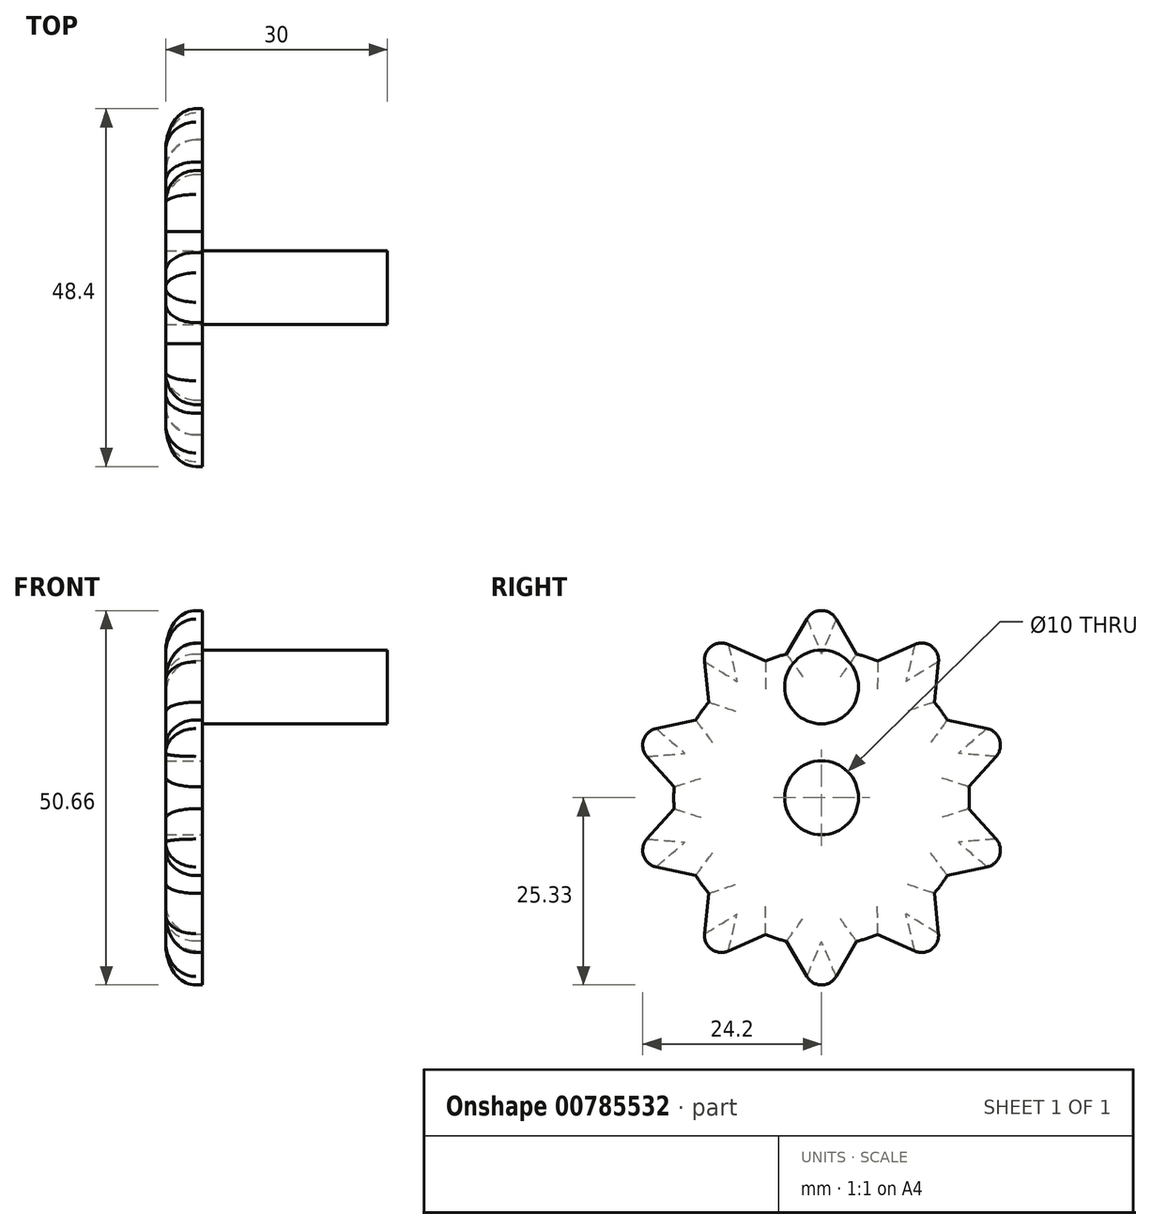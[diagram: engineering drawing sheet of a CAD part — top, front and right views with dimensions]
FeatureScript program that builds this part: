
annotation { "Feature Type Name" : "Feature", "Feature Type Description" : "" }
export const myFeature = defineFeature(function(context is Context, id is Id, definition is map)
    precondition{}
    {
        {
            var Q0;
            Q0=qCreatedBy(makeId("Right.planeOp"),FACE);
            var sketch = newSketch(context, id + "F0", { "sketchPlane" : qUnion([Q0])});
            skCircle(sketch, "E0", {"center": v(0, 0) * mm, "radius": 5 * mm});
            skCircle(sketch, "E1", {"center": v(0, 0) * mm, "radius": 20 * mm});
            skSolve(sketch);
        }
        {
            var Q0;
            Q0 = qSketchRegion(id + "F0", true);
            extrude(context, id + "F1", {"entities" : qUnion([Q0]), "depth" : 5 * mm, "offsetDistance" : 25 * mm});
        }
        {
            var Q0;
            Q0=makeQuery(id+"F1.opExtrude","CAP_FACE",FACE,{"disambiguationData":[OSD([sQuery(id+"F0.wireOp",EDGE,"E0"),sQuery(id+"F0.wireOp",EDGE,"E1")])],"isStart":false});
            var sketch = newSketch(context, id + "F2", { "sketchPlane" : qUnion([Q0])});
            skLineSegment(sketch, "E2", {"start": v(-5, 19) * mm, "end": v(-1.99, 24.19) * mm});
            skLineSegment(sketch, "E3", {"start": v(-1.99, 24.19) * mm, "end": v(1.99, 24.19) * mm, "construction": true});
            skLineSegment(sketch, "E4", {"start": v(1.99, 24.19) * mm, "end": v(5, 19) * mm});
            skArc(sketch, "E5", {"start": v(1.99, 24.19) * mm, "mid": v(0, 25.33) * mm, "end": v(-1.99, 24.19) * mm});
            skPoint(sketch, "E6", {"position": v(0, 25.33) * mm});
            skLineSegment(sketch, "E7", {"start": v(5, 19) * mm, "end": v(6.17, 19) * mm});
            skLineSegment(sketch, "E8", {"start": v(-5, 19) * mm, "end": v(-6.17, 19) * mm});
            skLineSegment(sketch, "E9.1.0", {"start": v(-12.61, 20.73) * mm, "end": v(-7.12, 18.31) * mm});
            skLineSegment(sketch, "E9.1.1", {"start": v(-15.82, 18.4) * mm, "end": v(-12.61, 20.73) * mm, "construction": true});
            skLineSegment(sketch, "E9.1.2", {"start": v(-15.21, 12.43) * mm, "end": v(-15.82, 18.4) * mm});
            skArc(sketch, "E9.1.3", {"start": v(-12.61, 20.73) * mm, "mid": v(-14.89, 20.5) * mm, "end": v(-15.82, 18.4) * mm});
            skLineSegment(sketch, "E9.1.4", {"start": v(-7.12, 18.31) * mm, "end": v(-6.17, 19) * mm});
            skPoint(sketch, "E9.1.5", {"position": v(-14.89, 20.5) * mm});
            skLineSegment(sketch, "E9.1.6", {"start": v(-15.21, 12.43) * mm, "end": v(-16.17, 11.74) * mm});
            skLineSegment(sketch, "E9.2.0", {"start": v(-22.4, 9.36) * mm, "end": v(-16.52, 10.63) * mm});
            skLineSegment(sketch, "E9.2.1", {"start": v(-23.62, 5.59) * mm, "end": v(-22.4, 9.36) * mm, "construction": true});
            skLineSegment(sketch, "E9.2.2", {"start": v(-19.62, 1.12) * mm, "end": v(-23.62, 5.59) * mm});
            skArc(sketch, "E9.2.3", {"start": v(-22.4, 9.36) * mm, "mid": v(-24.09, 7.83) * mm, "end": v(-23.62, 5.59) * mm});
            skLineSegment(sketch, "E9.2.4", {"start": v(-16.52, 10.63) * mm, "end": v(-16.17, 11.74) * mm});
            skPoint(sketch, "E9.2.5", {"position": v(-24.09, 7.83) * mm});
            skLineSegment(sketch, "E9.2.6", {"start": v(-19.62, 1.12) * mm, "end": v(-19.98, 0) * mm});
            skLineSegment(sketch, "E9.3.0", {"start": v(-23.62, -5.59) * mm, "end": v(-19.62, -1.12) * mm});
            skLineSegment(sketch, "E9.3.1", {"start": v(-22.4, -9.36) * mm, "end": v(-23.62, -5.59) * mm, "construction": true});
            skLineSegment(sketch, "E9.3.2", {"start": v(-16.52, -10.63) * mm, "end": v(-22.4, -9.36) * mm});
            skArc(sketch, "E9.3.3", {"start": v(-23.62, -5.59) * mm, "mid": v(-24.09, -7.83) * mm, "end": v(-22.4, -9.36) * mm});
            skLineSegment(sketch, "E9.3.4", {"start": v(-19.62, -1.12) * mm, "end": v(-19.98, 0) * mm});
            skPoint(sketch, "E9.3.5", {"position": v(-24.09, -7.83) * mm});
            skLineSegment(sketch, "E9.3.6", {"start": v(-16.52, -10.63) * mm, "end": v(-16.17, -11.74) * mm});
            skLineSegment(sketch, "E9.4.0", {"start": v(-15.82, -18.4) * mm, "end": v(-15.21, -12.43) * mm});
            skLineSegment(sketch, "E9.4.1", {"start": v(-12.61, -20.73) * mm, "end": v(-15.82, -18.4) * mm, "construction": true});
            skLineSegment(sketch, "E9.4.2", {"start": v(-7.12, -18.31) * mm, "end": v(-12.61, -20.73) * mm});
            skArc(sketch, "E9.4.3", {"start": v(-15.82, -18.4) * mm, "mid": v(-14.89, -20.5) * mm, "end": v(-12.61, -20.73) * mm});
            skLineSegment(sketch, "E9.4.4", {"start": v(-15.21, -12.43) * mm, "end": v(-16.17, -11.74) * mm});
            skPoint(sketch, "E9.4.5", {"position": v(-14.89, -20.5) * mm});
            skLineSegment(sketch, "E9.4.6", {"start": v(-7.12, -18.31) * mm, "end": v(-6.17, -19) * mm});
            skLineSegment(sketch, "E9.5.0", {"start": v(-1.99, -24.19) * mm, "end": v(-5, -19) * mm});
            skLineSegment(sketch, "E9.5.1", {"start": v(1.99, -24.19) * mm, "end": v(-1.99, -24.19) * mm, "construction": true});
            skLineSegment(sketch, "E9.5.2", {"start": v(5, -19) * mm, "end": v(1.99, -24.19) * mm});
            skArc(sketch, "E9.5.3", {"start": v(-1.99, -24.19) * mm, "mid": v(0, -25.33) * mm, "end": v(1.99, -24.19) * mm});
            skLineSegment(sketch, "E9.5.4", {"start": v(-5, -19) * mm, "end": v(-6.17, -19) * mm});
            skPoint(sketch, "E9.5.5", {"position": v(0, -25.33) * mm});
            skLineSegment(sketch, "E9.5.6", {"start": v(5, -19) * mm, "end": v(6.17, -19) * mm});
            skLineSegment(sketch, "E9.6.0", {"start": v(12.61, -20.73) * mm, "end": v(7.12, -18.31) * mm});
            skLineSegment(sketch, "E9.6.1", {"start": v(15.82, -18.4) * mm, "end": v(12.61, -20.73) * mm, "construction": true});
            skLineSegment(sketch, "E9.6.2", {"start": v(15.21, -12.43) * mm, "end": v(15.82, -18.4) * mm});
            skArc(sketch, "E9.6.3", {"start": v(12.61, -20.73) * mm, "mid": v(14.89, -20.5) * mm, "end": v(15.82, -18.4) * mm});
            skLineSegment(sketch, "E9.6.4", {"start": v(7.12, -18.31) * mm, "end": v(6.17, -19) * mm});
            skPoint(sketch, "E9.6.5", {"position": v(14.89, -20.5) * mm});
            skLineSegment(sketch, "E9.6.6", {"start": v(15.21, -12.43) * mm, "end": v(16.17, -11.74) * mm});
            skLineSegment(sketch, "E9.7.0", {"start": v(22.4, -9.36) * mm, "end": v(16.52, -10.63) * mm});
            skLineSegment(sketch, "E9.7.1", {"start": v(23.62, -5.59) * mm, "end": v(22.4, -9.36) * mm, "construction": true});
            skLineSegment(sketch, "E9.7.2", {"start": v(19.62, -1.12) * mm, "end": v(23.62, -5.59) * mm});
            skArc(sketch, "E9.7.3", {"start": v(22.4, -9.36) * mm, "mid": v(24.09, -7.83) * mm, "end": v(23.62, -5.59) * mm});
            skLineSegment(sketch, "E9.7.4", {"start": v(16.52, -10.63) * mm, "end": v(16.17, -11.74) * mm});
            skPoint(sketch, "E9.7.5", {"position": v(24.09, -7.83) * mm});
            skLineSegment(sketch, "E9.7.6", {"start": v(19.62, -1.12) * mm, "end": v(19.98, 0) * mm});
            skLineSegment(sketch, "E9.8.0", {"start": v(23.62, 5.59) * mm, "end": v(19.62, 1.12) * mm});
            skLineSegment(sketch, "E9.8.1", {"start": v(22.4, 9.36) * mm, "end": v(23.62, 5.59) * mm, "construction": true});
            skLineSegment(sketch, "E9.8.2", {"start": v(16.52, 10.63) * mm, "end": v(22.4, 9.36) * mm});
            skArc(sketch, "E9.8.3", {"start": v(23.62, 5.59) * mm, "mid": v(24.09, 7.83) * mm, "end": v(22.4, 9.36) * mm});
            skLineSegment(sketch, "E9.8.4", {"start": v(19.62, 1.12) * mm, "end": v(19.98, 0) * mm});
            skPoint(sketch, "E9.8.5", {"position": v(24.09, 7.83) * mm});
            skLineSegment(sketch, "E9.8.6", {"start": v(16.52, 10.63) * mm, "end": v(16.17, 11.74) * mm});
            skLineSegment(sketch, "E9.9.0", {"start": v(15.82, 18.4) * mm, "end": v(15.21, 12.43) * mm});
            skLineSegment(sketch, "E9.9.1", {"start": v(12.61, 20.73) * mm, "end": v(15.82, 18.4) * mm, "construction": true});
            skLineSegment(sketch, "E9.9.2", {"start": v(7.12, 18.31) * mm, "end": v(12.61, 20.73) * mm});
            skArc(sketch, "E9.9.3", {"start": v(15.82, 18.4) * mm, "mid": v(14.89, 20.5) * mm, "end": v(12.61, 20.73) * mm});
            skLineSegment(sketch, "E9.9.4", {"start": v(15.21, 12.43) * mm, "end": v(16.17, 11.74) * mm});
            skPoint(sketch, "E9.9.5", {"position": v(14.89, 20.5) * mm});
            skLineSegment(sketch, "E9.9.6", {"start": v(7.12, 18.31) * mm, "end": v(6.17, 19) * mm});
            skPoint(sketch, "E9.center", {"position": v(0, 0) * mm});
            skSolve(sketch);
        }
        {
            var Q0;
            Q0 = qSketchRegion(id + "F2", true);
            extrude(context, id + "F3", {"entities" : qUnion([Q0]), "operationType" : NewBodyOperationType.ADD, "oppositeDirection" : true, "depth" : 5 * mm, "offsetDistance" : 25 * mm});
        }
        {
            var Q0;
            Q0=makeQuery(id+"F3.boolean.opBoolean","MERGE",FACE,{"derivedFrom":[makeQuery(id+"F1.opExtrude","CAP_FACE",FACE,{"disambiguationData":[OSD([sQuery(id+"F0.wireOp",EDGE,"E0"),sQuery(id+"F0.wireOp",EDGE,"E1")])],"isStart":false}),makeQuery(id+"F3.opExtrude","CAP_FACE",FACE,{"disambiguationData":[OSD([sQuery(id+"F2.wireOp",EDGE,"E2"),sQuery(id+"F2.wireOp",EDGE,"E4"),sQuery(id+"F2.wireOp",EDGE,"E5"),sQuery(id+"F2.wireOp",EDGE,"E7"),sQuery(id+"F2.wireOp",EDGE,"E8"),sQuery(id+"F2.wireOp",EDGE,"E9.1.0"),sQuery(id+"F2.wireOp",EDGE,"E9.1.2"),sQuery(id+"F2.wireOp",EDGE,"E9.1.3"),sQuery(id+"F2.wireOp",EDGE,"E9.1.4"),sQuery(id+"F2.wireOp",EDGE,"E9.1.6"),sQuery(id+"F2.wireOp",EDGE,"E9.2.0"),sQuery(id+"F2.wireOp",EDGE,"E9.2.2"),sQuery(id+"F2.wireOp",EDGE,"E9.2.3"),sQuery(id+"F2.wireOp",EDGE,"E9.2.4"),sQuery(id+"F2.wireOp",EDGE,"E9.2.6"),sQuery(id+"F2.wireOp",EDGE,"E9.3.0"),sQuery(id+"F2.wireOp",EDGE,"E9.3.2"),sQuery(id+"F2.wireOp",EDGE,"E9.3.3"),sQuery(id+"F2.wireOp",EDGE,"E9.3.4"),sQuery(id+"F2.wireOp",EDGE,"E9.3.6"),sQuery(id+"F2.wireOp",EDGE,"E9.4.0"),sQuery(id+"F2.wireOp",EDGE,"E9.4.2"),sQuery(id+"F2.wireOp",EDGE,"E9.4.3"),sQuery(id+"F2.wireOp",EDGE,"E9.4.4"),sQuery(id+"F2.wireOp",EDGE,"E9.4.6"),sQuery(id+"F2.wireOp",EDGE,"E9.5.0"),sQuery(id+"F2.wireOp",EDGE,"E9.5.2"),sQuery(id+"F2.wireOp",EDGE,"E9.5.3"),sQuery(id+"F2.wireOp",EDGE,"E9.5.4"),sQuery(id+"F2.wireOp",EDGE,"E9.5.6"),sQuery(id+"F2.wireOp",EDGE,"E9.6.0"),sQuery(id+"F2.wireOp",EDGE,"E9.6.2"),sQuery(id+"F2.wireOp",EDGE,"E9.6.3"),sQuery(id+"F2.wireOp",EDGE,"E9.6.4"),sQuery(id+"F2.wireOp",EDGE,"E9.6.6"),sQuery(id+"F2.wireOp",EDGE,"E9.7.0"),sQuery(id+"F2.wireOp",EDGE,"E9.7.2"),sQuery(id+"F2.wireOp",EDGE,"E9.7.3"),sQuery(id+"F2.wireOp",EDGE,"E9.7.4"),sQuery(id+"F2.wireOp",EDGE,"E9.7.6"),sQuery(id+"F2.wireOp",EDGE,"E9.8.0"),sQuery(id+"F2.wireOp",EDGE,"E9.8.2"),sQuery(id+"F2.wireOp",EDGE,"E9.8.3"),sQuery(id+"F2.wireOp",EDGE,"E9.8.4"),sQuery(id+"F2.wireOp",EDGE,"E9.8.6"),sQuery(id+"F2.wireOp",EDGE,"E9.9.0"),sQuery(id+"F2.wireOp",EDGE,"E9.9.2"),sQuery(id+"F2.wireOp",EDGE,"E9.9.3"),sQuery(id+"F2.wireOp",EDGE,"E9.9.4"),sQuery(id+"F2.wireOp",EDGE,"E9.9.6"),sQuery(id+"F2.wireOp",EDGE,"E9.10.0"),sQuery(id+"F2.wireOp",EDGE,"E9.10.2"),sQuery(id+"F2.wireOp",EDGE,"E9.10.3"),sQuery(id+"F2.wireOp",EDGE,"E9.10.4"),sQuery(id+"F2.wireOp",EDGE,"E9.10.6"),sQuery(id+"F2.wireOp",EDGE,"E9.11.0"),sQuery(id+"F2.wireOp",EDGE,"E9.11.2"),sQuery(id+"F2.wireOp",EDGE,"E9.11.3"),sQuery(id+"F2.wireOp",EDGE,"E9.11.4"),sQuery(id+"F2.wireOp",EDGE,"E9.11.6"),sQuery(id+"F2.wireOp",EDGE,"E9.12.0"),sQuery(id+"F2.wireOp",EDGE,"E9.12.2"),sQuery(id+"F2.wireOp",EDGE,"E9.12.3"),sQuery(id+"F2.wireOp",EDGE,"E9.12.4"),sQuery(id+"F2.wireOp",EDGE,"E9.12.6"),sQuery(id+"F2.wireOp",EDGE,"E9.13.0"),sQuery(id+"F2.wireOp",EDGE,"E9.13.2"),sQuery(id+"F2.wireOp",EDGE,"E9.13.3"),sQuery(id+"F2.wireOp",EDGE,"E9.13.4"),sQuery(id+"F2.wireOp",EDGE,"E9.13.6"),sQuery(id+"F2.wireOp",EDGE,"86ff9663-5357-4066-ba58-08257a1c8855.6.14.0"),sQuery(id+"F2.wireOp",EDGE,"86ff9663-5357-4066-ba58-08257a1c8855.9.14.0"),sQuery(id+"F2.wireOp",EDGE,"86ff9663-5357-4066-ba58-08257a1c8855.13.14.0"),sQuery(id+"F2.wireOp",EDGE,"86ff9663-5357-4066-ba58-08257a1c8855.17.14.0"),sQuery(id+"F2.wireOp",EDGE,"86ff9663-5357-4066-ba58-08257a1c8855.19.14.0")])],"isStart":true})]});
            var sketch = newSketch(context, id + "F4", { "sketchPlane" : qUnion([Q0])});
            skCircle(sketch, "E10", {"center": v(0, 0) * mm, "radius": 5 * mm});
            skSolve(sketch);
        }
        {
            var Q0;
            Q0 = qSketchRegion(id + "F4", true);
            extrude(context, id + "F5", {"entities" : qUnion([Q0]), "operationType" : NewBodyOperationType.REMOVE, "endBound" : BoundingType.THROUGH_ALL, "oppositeDirection" : true, "depth" : 25 * mm, "offsetDistance" : 25 * mm});
        }
        {
            var Q0;
            Q0=makeQuery(id+"F3.opExtrude","CAP_EDGE",EDGE,{"disambiguationData":[OSD([sQuery(id+"F2.wireOp",EDGE,"E9.8.0")])],"isStart":false});
            var Q1;
            Q1=makeQuery(id+"F3.opExtrude","CAP_EDGE",EDGE,{"disambiguationData":[OSD([sQuery(id+"F2.wireOp",EDGE,"E9.9.3")])],"isStart":false});
            var Q2;
            Q2=makeQuery(id+"F3.opExtrude","CAP_EDGE",EDGE,{"disambiguationData":[OSD([sQuery(id+"F2.wireOp",EDGE,"E4")])],"isStart":false});
            var Q3;
            Q3=makeQuery(id+"F3.opExtrude","CAP_EDGE",EDGE,{"disambiguationData":[OSD([sQuery(id+"F2.wireOp",EDGE,"E9.7.3")])],"isStart":false});
            var Q4;
            {var subQ1=sQuery(id+"F2.wireOp",EDGE,"E9.7.2");var subQ2=sQuery(id+"F0.wireOp",EDGE,"E1");Q4=makeQuery(id+"F3.boolean.opBoolean","SPLIT",EDGE,{"disambiguationData":[TD([makeQuery(id+"F3.opExtrude","SWEPT_FACE",FACE,{"disambiguationData":[OSD([subQ1])]})])],"derivedFrom":makeQuery(id+"F1.opExtrude","CAP_EDGE",EDGE,{"disambiguationData":[OSD([subQ2])],"isStart":true})});}
            var Q5;
            Q5=makeQuery(id+"F3.opExtrude","CAP_EDGE",EDGE,{"disambiguationData":[OSD([sQuery(id+"F2.wireOp",EDGE,"E9.6.2")])],"isStart":false});
            var Q6;
            Q6=makeQuery(id+"F3.opExtrude","CAP_EDGE",EDGE,{"disambiguationData":[OSD([sQuery(id+"F2.wireOp",EDGE,"E9.6.3")])],"isStart":false});
            var Q7;
            Q7=makeQuery(id+"F3.opExtrude","CAP_EDGE",EDGE,{"disambiguationData":[OSD([sQuery(id+"F2.wireOp",EDGE,"E9.8.3")])],"isStart":false});
            var Q8;
            Q8=makeQuery(id+"F3.opExtrude","CAP_EDGE",EDGE,{"disambiguationData":[OSD([sQuery(id+"F2.wireOp",EDGE,"E9.9.0")])],"isStart":false});
            var Q9;
            Q9=makeQuery(id+"F3.opExtrude","CAP_EDGE",EDGE,{"disambiguationData":[OSD([sQuery(id+"F2.wireOp",EDGE,"E9.5.2")])],"isStart":false});
            var Q10;
            Q10=makeQuery(id+"F3.opExtrude","CAP_EDGE",EDGE,{"disambiguationData":[OSD([sQuery(id+"F2.wireOp",EDGE,"E9.1.2")])],"isStart":false});
            var Q11;
            Q11=makeQuery(id+"F3.opExtrude","CAP_EDGE",EDGE,{"disambiguationData":[OSD([sQuery(id+"F2.wireOp",EDGE,"E9.8.2")])],"isStart":false});
            var Q12;
            Q12=makeQuery(id+"F3.opExtrude","CAP_EDGE",EDGE,{"disambiguationData":[OSD([sQuery(id+"F2.wireOp",EDGE,"E9.3.3")])],"isStart":false});
            var Q13;
            Q13=makeQuery(id+"F3.opExtrude","CAP_EDGE",EDGE,{"disambiguationData":[OSD([sQuery(id+"F2.wireOp",EDGE,"E9.7.0")])],"isStart":false});
            var Q14;
            Q14=makeQuery(id+"F3.opExtrude","CAP_EDGE",EDGE,{"disambiguationData":[OSD([sQuery(id+"F2.wireOp",EDGE,"E2")])],"isStart":false});
            var Q15;
            Q15=makeQuery(id+"F3.opExtrude","CAP_EDGE",EDGE,{"disambiguationData":[OSD([sQuery(id+"F2.wireOp",EDGE,"E9.7.2")])],"isStart":false});
            var Q16;
            Q16=makeQuery(id+"F3.opExtrude","CAP_EDGE",EDGE,{"disambiguationData":[OSD([sQuery(id+"F2.wireOp",EDGE,"E9.5.0")])],"isStart":false});
            var Q17;
            Q17=makeQuery(id+"F3.opExtrude","CAP_EDGE",EDGE,{"disambiguationData":[OSD([sQuery(id+"F2.wireOp",EDGE,"E5")])],"isStart":false});
            var Q18;
            Q18=makeQuery(id+"F3.opExtrude","CAP_EDGE",EDGE,{"disambiguationData":[OSD([sQuery(id+"F2.wireOp",EDGE,"E9.4.0")])],"isStart":false});
            var Q19;
            Q19=makeQuery(id+"F3.opExtrude","CAP_EDGE",EDGE,{"disambiguationData":[OSD([sQuery(id+"F2.wireOp",EDGE,"E9.6.0")])],"isStart":false});
            var Q20;
            Q20=makeQuery(id+"F3.opExtrude","CAP_EDGE",EDGE,{"disambiguationData":[OSD([sQuery(id+"F2.wireOp",EDGE,"E9.5.3")])],"isStart":false});
            var Q21;
            {var subQ1=sQuery(id+"F2.wireOp",EDGE,"E9.6.2");var subQ2=sQuery(id+"F0.wireOp",EDGE,"E1");Q21=makeQuery(id+"F3.boolean.opBoolean","SPLIT",EDGE,{"disambiguationData":[TD([makeQuery(id+"F3.opExtrude","SWEPT_FACE",FACE,{"disambiguationData":[OSD([subQ1])]})])],"derivedFrom":makeQuery(id+"F1.opExtrude","CAP_EDGE",EDGE,{"disambiguationData":[OSD([subQ2])],"isStart":true})});}
            var Q22;
            {var subQ1=sQuery(id+"F2.wireOp",EDGE,"E9.8.2");var subQ2=sQuery(id+"F0.wireOp",EDGE,"E1");Q22=makeQuery(id+"F3.boolean.opBoolean","SPLIT",EDGE,{"disambiguationData":[TD([makeQuery(id+"F3.opExtrude","SWEPT_FACE",FACE,{"disambiguationData":[OSD([subQ1])]})])],"derivedFrom":makeQuery(id+"F1.opExtrude","CAP_EDGE",EDGE,{"disambiguationData":[OSD([subQ2])],"isStart":true})});}
            var Q23;
            Q23=makeQuery(id+"F3.opExtrude","CAP_EDGE",EDGE,{"disambiguationData":[OSD([sQuery(id+"F2.wireOp",EDGE,"E9.9.2")])],"isStart":false});
            var Q24;
            Q24=makeQuery(id+"F3.opExtrude","CAP_EDGE",EDGE,{"disambiguationData":[OSD([sQuery(id+"F2.wireOp",EDGE,"E9.2.3")])],"isStart":false});
            var Q25;
            {var subQ1=sQuery(id+"F2.wireOp",EDGE,"E9.2.2");var subQ2=sQuery(id+"F0.wireOp",EDGE,"E1");Q25=makeQuery(id+"F3.boolean.opBoolean","SPLIT",EDGE,{"disambiguationData":[TD([makeQuery(id+"F3.opExtrude","SWEPT_FACE",FACE,{"disambiguationData":[OSD([subQ1])]})])],"derivedFrom":makeQuery(id+"F1.opExtrude","CAP_EDGE",EDGE,{"disambiguationData":[OSD([subQ2])],"isStart":true})});}
            var Q26;
            Q26=makeQuery(id+"F3.opExtrude","CAP_EDGE",EDGE,{"disambiguationData":[OSD([sQuery(id+"F2.wireOp",EDGE,"E9.3.0")])],"isStart":false});
            var Q27;
            {var subQ1=sQuery(id+"F2.wireOp",EDGE,"E9.5.2");var subQ2=sQuery(id+"F0.wireOp",EDGE,"E1");Q27=makeQuery(id+"F3.boolean.opBoolean","SPLIT",EDGE,{"disambiguationData":[TD([makeQuery(id+"F3.opExtrude","SWEPT_FACE",FACE,{"disambiguationData":[OSD([subQ1])]})])],"derivedFrom":makeQuery(id+"F1.opExtrude","CAP_EDGE",EDGE,{"disambiguationData":[OSD([subQ2])],"isStart":true})});}
            var Q28;
            {var subQ1=sQuery(id+"F2.wireOp",EDGE,"E9.1.2");var subQ2=sQuery(id+"F0.wireOp",EDGE,"E1");Q28=makeQuery(id+"F3.boolean.opBoolean","SPLIT",EDGE,{"disambiguationData":[TD([makeQuery(id+"F3.opExtrude","SWEPT_FACE",FACE,{"disambiguationData":[OSD([subQ1])]})])],"derivedFrom":makeQuery(id+"F1.opExtrude","CAP_EDGE",EDGE,{"disambiguationData":[OSD([subQ2])],"isStart":true})});}
            var Q29;
            {var subQ1=sQuery(id+"F2.wireOp",EDGE,"E9.3.2");var subQ2=sQuery(id+"F0.wireOp",EDGE,"E1");Q29=makeQuery(id+"F3.boolean.opBoolean","SPLIT",EDGE,{"disambiguationData":[TD([makeQuery(id+"F3.opExtrude","SWEPT_FACE",FACE,{"disambiguationData":[OSD([subQ1])]})])],"derivedFrom":makeQuery(id+"F1.opExtrude","CAP_EDGE",EDGE,{"disambiguationData":[OSD([subQ2])],"isStart":true})});}
            var Q30;
            {var subQ1=sQuery(id+"F2.wireOp",EDGE,"E4");var subQ2=sQuery(id+"F0.wireOp",EDGE,"E1");Q30=makeQuery(id+"F3.boolean.opBoolean","SPLIT",EDGE,{"disambiguationData":[TD([makeQuery(id+"F3.opExtrude","SWEPT_FACE",FACE,{"disambiguationData":[OSD([subQ1])]})])],"derivedFrom":makeQuery(id+"F1.opExtrude","CAP_EDGE",EDGE,{"disambiguationData":[OSD([subQ2])],"isStart":true})});}
            var Q31;
            Q31=makeQuery(id+"F3.opExtrude","CAP_EDGE",EDGE,{"disambiguationData":[OSD([sQuery(id+"F2.wireOp",EDGE,"E9.1.3")])],"isStart":false});
            var Q32;
            Q32=makeQuery(id+"F3.opExtrude","CAP_EDGE",EDGE,{"disambiguationData":[OSD([sQuery(id+"F2.wireOp",EDGE,"E9.2.0")])],"isStart":false});
            var Q33;
            Q33=makeQuery(id+"F3.opExtrude","CAP_EDGE",EDGE,{"disambiguationData":[OSD([sQuery(id+"F2.wireOp",EDGE,"E9.3.2")])],"isStart":false});
            var Q34;
            Q34=makeQuery(id+"F3.opExtrude","CAP_EDGE",EDGE,{"disambiguationData":[OSD([sQuery(id+"F2.wireOp",EDGE,"E9.2.2")])],"isStart":false});
            var Q35;
            Q35=makeQuery(id+"F3.opExtrude","CAP_EDGE",EDGE,{"disambiguationData":[OSD([sQuery(id+"F2.wireOp",EDGE,"E9.1.0")])],"isStart":false});
            var Q36;
            {var subQ1=sQuery(id+"F2.wireOp",EDGE,"E2");var subQ2=sQuery(id+"F0.wireOp",EDGE,"E1");Q36=makeQuery(id+"F3.boolean.opBoolean","SPLIT",EDGE,{"disambiguationData":[TD([makeQuery(id+"F3.opExtrude","SWEPT_FACE",FACE,{"disambiguationData":[OSD([subQ1])]})])],"derivedFrom":makeQuery(id+"F1.opExtrude","CAP_EDGE",EDGE,{"disambiguationData":[OSD([subQ2])],"isStart":true})});}
            var Q37;
            {var subQ1=sQuery(id+"F2.wireOp",EDGE,"E9.4.2");var subQ2=sQuery(id+"F0.wireOp",EDGE,"E1");Q37=makeQuery(id+"F3.boolean.opBoolean","SPLIT",EDGE,{"disambiguationData":[TD([makeQuery(id+"F3.opExtrude","SWEPT_FACE",FACE,{"disambiguationData":[OSD([subQ1])]})])],"derivedFrom":makeQuery(id+"F1.opExtrude","CAP_EDGE",EDGE,{"disambiguationData":[OSD([subQ2])],"isStart":true})});}
            var Q38;
            Q38=makeQuery(id+"F3.opExtrude","CAP_EDGE",EDGE,{"disambiguationData":[OSD([sQuery(id+"F2.wireOp",EDGE,"E9.4.2")])],"isStart":false});
            var Q39;
            Q39=makeQuery(id+"F3.opExtrude","CAP_EDGE",EDGE,{"disambiguationData":[OSD([sQuery(id+"F2.wireOp",EDGE,"E9.4.3")])],"isStart":false});
            fillet(context, id + "F6", {"entities" : qUnion([Q0, Q1, Q2, Q3, Q4, Q5, Q6, Q7, Q8, Q9, Q10, Q11, Q12, Q13, Q14, Q15, Q16, Q17, Q18, Q19, Q20, Q21, Q22, Q23, Q24, Q25, Q26, Q27, Q28, Q29, Q30, Q31, Q32, Q33, Q34, Q35, Q36, Q37, Q38, Q39]), "radius" : 4.1 * mm, "tangentPropagation" : true, "allowEdgeOverflow" : false});
        }
        {
            var Q0;
            Q0=makeQuery(id+"F3.boolean.opBoolean","MERGE",FACE,{"derivedFrom":[makeQuery(id+"F1.opExtrude","CAP_FACE",FACE,{"disambiguationData":[OSD([sQuery(id+"F0.wireOp",EDGE,"E0"),sQuery(id+"F0.wireOp",EDGE,"E1")])],"isStart":false}),makeQuery(id+"F3.opExtrude","CAP_FACE",FACE,{"disambiguationData":[OSD([sQuery(id+"F2.wireOp",EDGE,"E2"),sQuery(id+"F2.wireOp",EDGE,"E4"),sQuery(id+"F2.wireOp",EDGE,"E5"),sQuery(id+"F2.wireOp",EDGE,"E7"),sQuery(id+"F2.wireOp",EDGE,"E8"),sQuery(id+"F2.wireOp",EDGE,"E9.1.0"),sQuery(id+"F2.wireOp",EDGE,"E9.1.2"),sQuery(id+"F2.wireOp",EDGE,"E9.1.3"),sQuery(id+"F2.wireOp",EDGE,"E9.1.4"),sQuery(id+"F2.wireOp",EDGE,"E9.1.6"),sQuery(id+"F2.wireOp",EDGE,"E9.2.0"),sQuery(id+"F2.wireOp",EDGE,"E9.2.2"),sQuery(id+"F2.wireOp",EDGE,"E9.2.3"),sQuery(id+"F2.wireOp",EDGE,"E9.2.4"),sQuery(id+"F2.wireOp",EDGE,"E9.2.6"),sQuery(id+"F2.wireOp",EDGE,"E9.3.0"),sQuery(id+"F2.wireOp",EDGE,"E9.3.2"),sQuery(id+"F2.wireOp",EDGE,"E9.3.3"),sQuery(id+"F2.wireOp",EDGE,"E9.3.4"),sQuery(id+"F2.wireOp",EDGE,"E9.3.6"),sQuery(id+"F2.wireOp",EDGE,"E9.4.0"),sQuery(id+"F2.wireOp",EDGE,"E9.4.2"),sQuery(id+"F2.wireOp",EDGE,"E9.4.3"),sQuery(id+"F2.wireOp",EDGE,"E9.4.4"),sQuery(id+"F2.wireOp",EDGE,"E9.4.6"),sQuery(id+"F2.wireOp",EDGE,"E9.5.0"),sQuery(id+"F2.wireOp",EDGE,"E9.5.2"),sQuery(id+"F2.wireOp",EDGE,"E9.5.3"),sQuery(id+"F2.wireOp",EDGE,"E9.5.4"),sQuery(id+"F2.wireOp",EDGE,"E9.5.6"),sQuery(id+"F2.wireOp",EDGE,"E9.6.0"),sQuery(id+"F2.wireOp",EDGE,"E9.6.2"),sQuery(id+"F2.wireOp",EDGE,"E9.6.3"),sQuery(id+"F2.wireOp",EDGE,"E9.6.4"),sQuery(id+"F2.wireOp",EDGE,"E9.6.6"),sQuery(id+"F2.wireOp",EDGE,"E9.7.0"),sQuery(id+"F2.wireOp",EDGE,"E9.7.2"),sQuery(id+"F2.wireOp",EDGE,"E9.7.3"),sQuery(id+"F2.wireOp",EDGE,"E9.7.4"),sQuery(id+"F2.wireOp",EDGE,"E9.7.6"),sQuery(id+"F2.wireOp",EDGE,"E9.8.0"),sQuery(id+"F2.wireOp",EDGE,"E9.8.2"),sQuery(id+"F2.wireOp",EDGE,"E9.8.3"),sQuery(id+"F2.wireOp",EDGE,"E9.8.4"),sQuery(id+"F2.wireOp",EDGE,"E9.8.6"),sQuery(id+"F2.wireOp",EDGE,"E9.9.0"),sQuery(id+"F2.wireOp",EDGE,"E9.9.2"),sQuery(id+"F2.wireOp",EDGE,"E9.9.3"),sQuery(id+"F2.wireOp",EDGE,"E9.9.4"),sQuery(id+"F2.wireOp",EDGE,"E9.9.6")])],"isStart":true})]});
            var sketch = newSketch(context, id + "F7", { "sketchPlane" : qUnion([Q0])});
            skCircle(sketch, "E11", {"center": v(0, 15) * mm, "radius": 5 * mm});
            skSolve(sketch);
        }
        {
            var Q0;
            Q0 = qSketchRegion(id + "F7", true);
            extrude(context, id + "F8", {"entities" : qUnion([Q0]), "operationType" : NewBodyOperationType.ADD, "depth" : 25 * mm, "offsetDistance" : 25 * mm});
        }
    });
